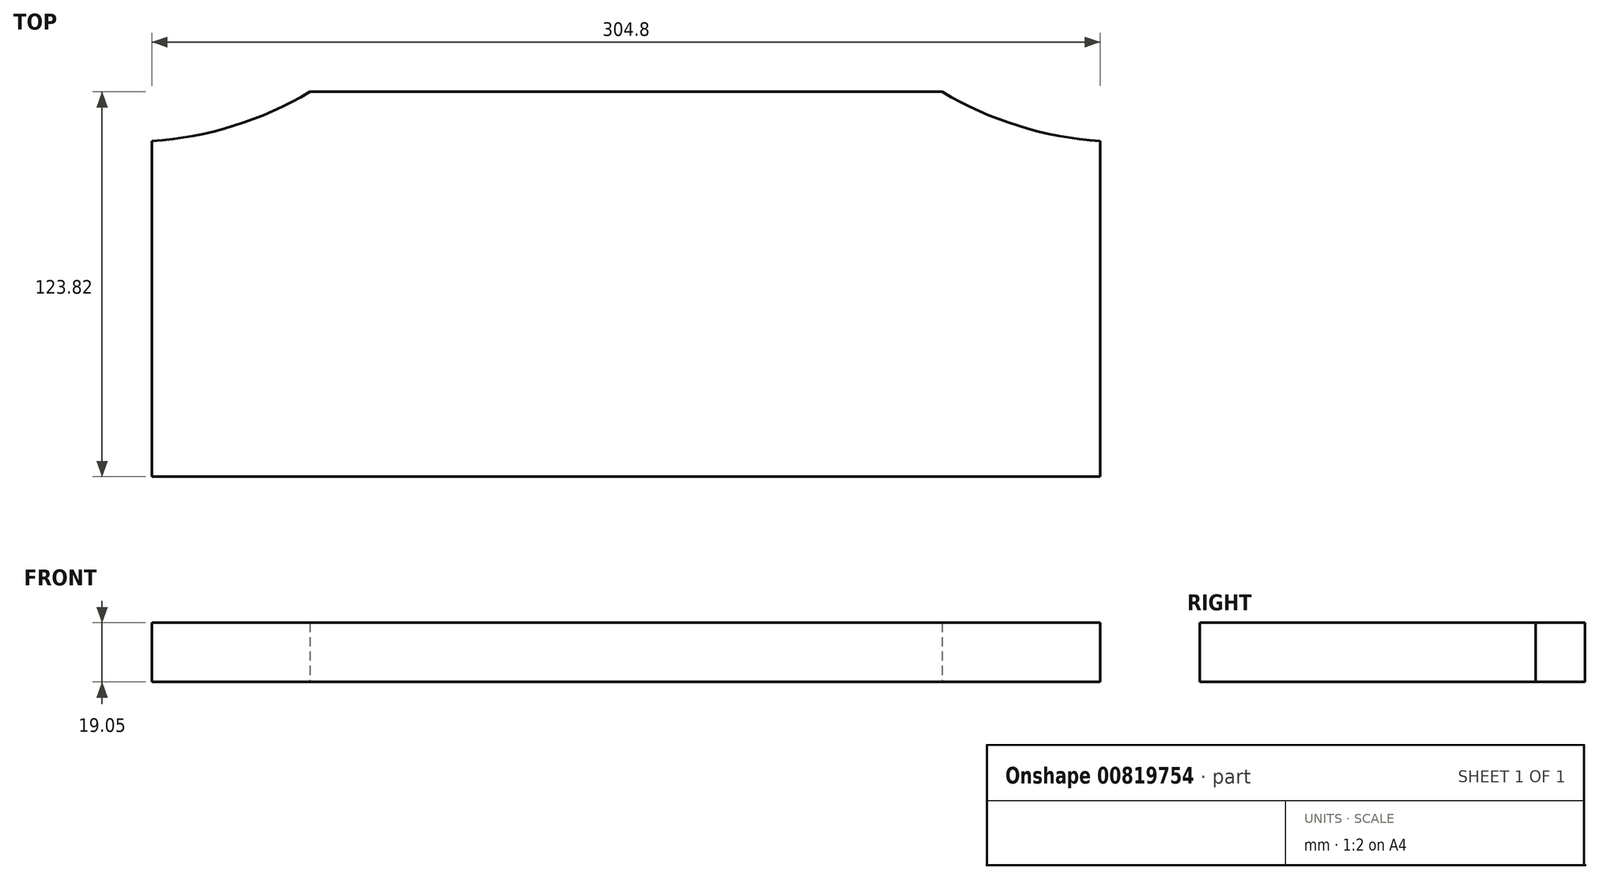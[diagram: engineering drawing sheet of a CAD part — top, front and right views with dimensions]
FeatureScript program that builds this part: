
annotation { "Feature Type Name" : "Feature", "Feature Type Description" : "" }
export const myFeature = defineFeature(function(context is Context, id is Id, definition is map)
    precondition{}
    {
        {
            var Q0;
            Q0=qCreatedBy(makeId("Top.planeOp"),FACE);
            var sketch = newSketch(context, id + "F0", { "sketchPlane" : qUnion([Q0])});
            skLineSegment(sketch, "E0.bottom", {"start": v(152.4, -61.91) * mm, "end": v(-152.4, -61.91) * mm});
            skLineSegment(sketch, "E0.top", {"start": v(101.6, 61.91) * mm, "end": v(-101.6, 61.91) * mm});
            skLineSegment(sketch, "E0.left", {"start": v(152.4, -61.91) * mm, "end": v(152.4, 46.04) * mm});
            skLineSegment(sketch, "E0.right", {"start": v(-152.4, -61.91) * mm, "end": v(-152.4, 46.04) * mm});
            skPoint(sketch, "E0.middle", {"position": v(0, 0) * mm});
            skArc(sketch, "E1", {"start": v(101.6, 61.91) * mm, "mid": v(126.06, 50.98) * mm, "end": v(152.4, 46.04) * mm});
            skLineSegment(sketch, "E2.MirrorCS", {"start": v(-101.6, 61.91) * mm, "end": v(101.6, 61.91) * mm});
            skArc(sketch, "E3.MirrorC", {"start": v(-101.6, 61.91) * mm, "mid": v(-126.06, 50.98) * mm, "end": v(-152.4, 46.04) * mm});
            skSolve(sketch);
        }
        {
            var Q0;
            Q0 = qSketchRegion(id + "F0", true);
            extrude(context, id + "F1", {"entities" : qUnion([Q0]), "depth" : 19.05 * mm, "offsetDistance" : 25.4 * mm});
        }
    });
